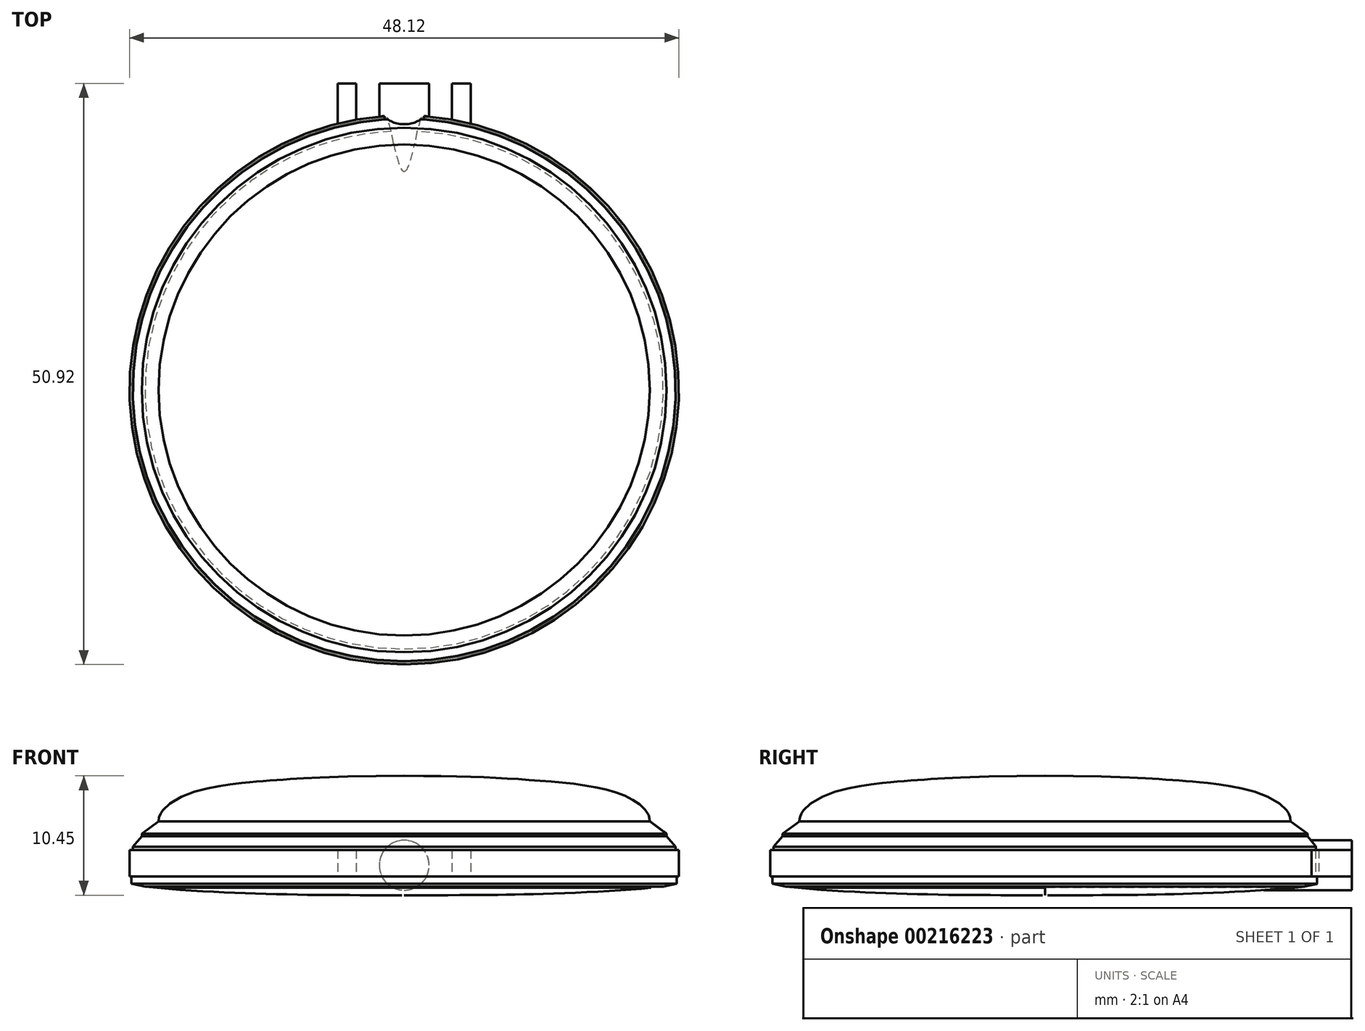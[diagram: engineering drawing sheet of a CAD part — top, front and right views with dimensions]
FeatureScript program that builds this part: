
annotation { "Feature Type Name" : "Feature", "Feature Type Description" : "" }
export const myFeature = defineFeature(function(context is Context, id is Id, definition is map)
    precondition{}
    {
        {
            var Q0;
            Q0=qCreatedBy(makeId("Top.planeOp"),FACE);
            var sketch = newSketch(context, id + "F0", { "sketchPlane" : qUnion([Q0])});
            skCircle(sketch, "E0", {"center": v(0, 0) * mm, "radius": 24.06 * mm});
            skSolve(sketch);
        }
        {
            var Q0;
            Q0 = qSketchRegion(id + "F0", true);
            extrude(context, id + "F1", {"entities" : qUnion([Q0]), "depth" : 2.32 * mm});
        }
        {
            var Q0;
            Q0=qCreatedBy(makeId("Front.planeOp"),FACE);
            var sketch = newSketch(context, id + "F2", { "sketchPlane" : qUnion([Q0])});
            skLineSegment(sketch, "E1", {"start": v(0, 66.42) * mm, "end": v(0, -62.07) * mm, "construction": true});
            skFitSpline(sketch, "E2", {"points": [v(0, -1.65) * mm, v(10.95, -1.56) * mm, v(21.63, -1) * mm], "startDerivative": vector(34.83, 0) * mm, "endDerivative": vector(19.05, 1.97) * mm});
            skLineSegment(sketch, "E3", {"start": v(23.88, 0) * mm, "end": v(23.88, -0.66) * mm});
            skLineSegment(sketch, "E4", {"start": v(23.88, -0.66) * mm, "end": v(22.7, -0.9) * mm});
            skLineSegment(sketch, "E5", {"start": v(22.7, -0.9) * mm, "end": v(21.63, -1) * mm});
            skLineSegment(sketch, "E6", {"start": v(0, -1.65) * mm, "end": v(0, 0) * mm});
            skLineSegment(sketch, "E7", {"start": v(0, 0) * mm, "end": v(23.88, 0) * mm});
            skSolve(sketch);
        }
        {
            var Q0;
            Q0 = qSketchRegion(id + "F2", true);
            var Q1;
            Q1=sQuery(id+"F2.wireOp",EDGE,"E1");
            revolve(context, id + "F3", {"operationType" : NewBodyOperationType.ADD, "entities" : qUnion([Q0]), "axis" : qUnion([Q1]), "revolveType" : RevolveType.FULL});
        }
        {
            var Q0;
            Q0=qCreatedBy(makeId("Front.planeOp"),FACE);
            var sketch = newSketch(context, id + "F4", { "sketchPlane" : qUnion([Q0])});
            skLineSegment(sketch, "E8", {"start": v(23.77, 2.32) * mm, "end": v(23.77, 2.6) * mm});
            skLineSegment(sketch, "E9", {"start": v(23.77, 2.6) * mm, "end": v(22.98, 3.5) * mm});
            skLineSegment(sketch, "E10", {"start": v(22.98, 3.5) * mm, "end": v(22.98, 3.74) * mm});
            skLineSegment(sketch, "E11", {"start": v(22.98, 3.74) * mm, "end": v(21.5, 4.82) * mm});
            skLineSegment(sketch, "E12", {"start": v(21.5, 4.82) * mm, "end": v(0, 4.82) * mm});
            skLineSegment(sketch, "E13", {"start": v(0, 4.82) * mm, "end": v(0, 2.32) * mm});
            skLineSegment(sketch, "E14", {"start": v(0, 2.32) * mm, "end": v(23.77, 2.32) * mm});
            skSolve(sketch);
        }
        {
            var Q0;
            Q0 = qSketchRegion(id + "F4", true);
            var Q1;
            Q1=sQuery(id+"F2.wireOp",EDGE,"E1");
            revolve(context, id + "F5", {"operationType" : NewBodyOperationType.ADD, "entities" : qUnion([Q0]), "axis" : qUnion([Q1]), "revolveType" : RevolveType.FULL});
        }
        {
            var Q0;
            Q0=qCreatedBy(makeId("Front.planeOp"),FACE);
            var sketch = newSketch(context, id + "F6", { "sketchPlane" : qUnion([Q0])});
            skFitSpline(sketch, "E15", {"points": [v(21.51, 4.82) * mm, v(19.12, 7.14) * mm, v(11.78, 8.39) * mm, v(0, 8.8) * mm], "startDerivative": vector(0, 12.59) * mm, "endDerivative": vector(-41.08, 0) * mm});
            skLineSegment(sketch, "E16", {"start": v(0, 8.8) * mm, "end": v(0, 4.82) * mm});
            skLineSegment(sketch, "E17", {"start": v(0, 4.82) * mm, "end": v(21.51, 4.82) * mm});
            skSolve(sketch);
        }
        {
            var Q0;
            Q0 = qSketchRegion(id + "F6", true);
            var Q1;
            Q1=sQuery(id+"F2.wireOp",EDGE,"E1");
            revolve(context, id + "F7", {"operationType" : NewBodyOperationType.ADD, "entities" : qUnion([Q0]), "axis" : qUnion([Q1]), "revolveType" : RevolveType.FULL});
        }
        {
            var Q0;
            Q0=qCreatedBy(makeId("Top.planeOp"),FACE);
            var sketch = newSketch(context, id + "F8", { "sketchPlane" : qUnion([Q0])});
            skLineSegment(sketch, "E18", {"start": v(0, 37.72) * mm, "end": v(0, 2.03) * mm, "construction": true});
            skLineSegment(sketch, "E19", {"start": v(4.2, 23.69) * mm, "end": v(4.2, 26.86) * mm});
            skLineSegment(sketch, "E20", {"start": v(4.2, 26.86) * mm, "end": v(5.82, 26.86) * mm});
            skLineSegment(sketch, "E21", {"start": v(5.82, 26.86) * mm, "end": v(5.82, 23.34) * mm});
            skLineSegment(sketch, "E22", {"start": v(5.82, 23.34) * mm, "end": v(4.96, 22.06) * mm});
            skLineSegment(sketch, "E23", {"start": v(4.96, 22.06) * mm, "end": v(4.2, 23.69) * mm});
            skLineSegment(sketch, "E24.MirrorCS", {"start": v(-5.82, 23.34) * mm, "end": v(-4.96, 22.06) * mm});
            skLineSegment(sketch, "E25.MirrorCS", {"start": v(-5.82, 26.86) * mm, "end": v(-5.82, 23.34) * mm});
            skLineSegment(sketch, "E26.MirrorCS", {"start": v(-4.96, 22.06) * mm, "end": v(-4.19, 23.69) * mm});
            skLineSegment(sketch, "E27.MirrorCS", {"start": v(-4.19, 23.69) * mm, "end": v(-4.19, 26.86) * mm});
            skLineSegment(sketch, "E28.MirrorCS", {"start": v(-4.19, 26.86) * mm, "end": v(-5.82, 26.86) * mm});
            skCircle(sketch, "E29.0.0", {"center": v(0, 0) * mm, "radius": 24.06 * mm, "construction": true});
            skSolve(sketch);
        }
        {
            var Q0;
            Q0 = qSketchRegion(id + "F8", true);
            extrude(context, id + "F9", {"entities" : qUnion([Q0]), "operationType" : NewBodyOperationType.ADD, "depth" : 2.3 * mm});
        }
        {
            var Q0;
            Q0=qCreatedBy(makeId("Front.planeOp"),FACE);
            var sketch = newSketch(context, id + "F10", { "sketchPlane" : qUnion([Q0])});
            skLineSegment(sketch, "E30", {"start": v(0, 0) * mm, "end": v(0, 17.8) * mm, "construction": true});
            skCircle(sketch, "E31", {"center": v(0, 0.97) * mm, "radius": 2.19 * mm});
            skSolve(sketch);
        }
        {
            var Q0;
            Q0 = qSketchRegion(id + "F10", true);
            extrude(context, id + "F11", {"entities" : qUnion([Q0]), "operationType" : NewBodyOperationType.ADD, "oppositeDirection" : true, "depth" : 26.86 * mm});
        }
    });
